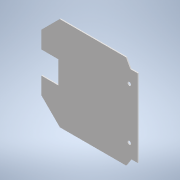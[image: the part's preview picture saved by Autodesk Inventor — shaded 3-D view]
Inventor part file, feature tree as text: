
AUTODESK INVENTOR PART (.ipt)
format: ipt  version: 2020 (Build 240168000, 168)  size: 154,112 bytes
history: native  units: mm
features: other x21, extrude x1, sketch x1
ambient origin geometry x8: Origin, YZ Plane, XZ Plane, XY Plane, X Axis, Y Axis, Z Axis, Center Point
bodies: Body1 (feature_tree)
feature tree (23):
  other  "Sólido1"
  extrude  "Extrusão1"  Depth=2.0mm
  sketch  "Esboço1"  dims[d3=1.5mm d4=0.0mm d16=2.0mm d17=2.0mm d20=45.0deg d21=45.0deg d22=2.0mm d24=0.0mm d25=24.0mm d26=16.0mm d23=0.872665mm]
  other  "Referência23"
  other  "Referência24"
  other  "Referência29"
  other  "Referência30"
  other  "Referência31"
  other  "Referência32"
  other  "Referência33"
  other  "Referência34"
  other  "Referência35"
  other  "<userpath>\Desktop\rabo\3d\ela.iam"
  other  "ela.iam"
  other  "apoio servo:1"
  other  "apoio servo_MIR:1"
  other  "basesinha:1"
  other  "Component2:4"
  other  "Component2:5"
  other  "Component2_7_MIR:3"
  other  "TCS230-TCS3200:1"
  other  "canto:1"
  other  "canto_MIR1:1"
